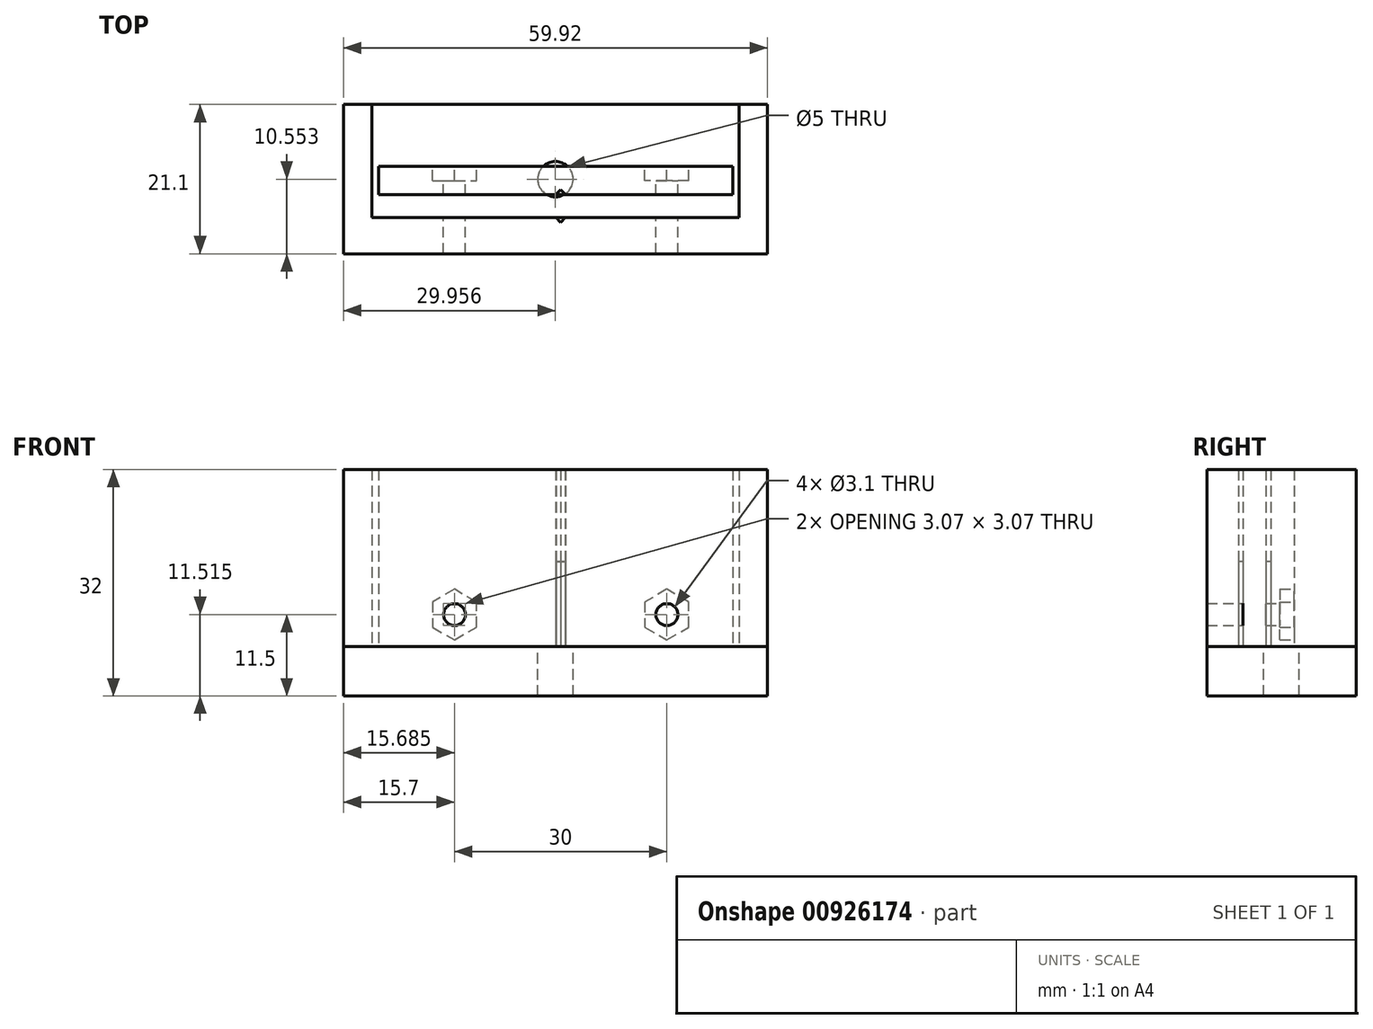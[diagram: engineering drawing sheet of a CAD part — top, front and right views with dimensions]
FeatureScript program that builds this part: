
annotation { "Feature Type Name" : "Feature", "Feature Type Description" : "" }
export const myFeature = defineFeature(function(context is Context, id is Id, definition is map)
    precondition{}
    {
        {
            var Q0;
            Q0=qCreatedBy(makeId("Top.planeOp"),FACE);
            var sketch = newSketch(context, id + "F0", { "sketchPlane" : qUnion([Q0])});
            skLineSegment(sketch, "E0.bottom", {"start": v(0, 1.43) * mm, "end": v(-0.7, 0.72) * mm});
            skLineSegment(sketch, "E0.top", {"start": v(0.7, 0.72) * mm, "end": v(0.7, 0.72) * mm});
            skLineSegment(sketch, "E0.left", {"start": v(0, 1.43) * mm, "end": v(0.7, 0.72) * mm});
            skLineSegment(sketch, "E0.right", {"start": v(-0.7, 0.72) * mm, "end": v(-0.7, 0.72) * mm});
            skLineSegment(sketch, "E1.bottom", {"start": v(24.3, 4.72) * mm, "end": v(-25.7, 4.72) * mm});
            skLineSegment(sketch, "E1.left", {"start": v(24.3, 4.72) * mm, "end": v(24.3, 0.72) * mm});
            skLineSegment(sketch, "E1.right", {"start": v(-25.7, 4.72) * mm, "end": v(-25.7, 0.71) * mm});
            skLineSegment(sketch, "E2", {"start": v(-25.7, 0.71) * mm, "end": v(-0.7, 0.72) * mm});
            skPoint(sketch, "E3", {"position": v(24.3, 0.72) * mm});
            skLineSegment(sketch, "E4.trimOffspring", {"start": v(0.7, 0.72) * mm, "end": v(24.3, 0.72) * mm});
            skPoint(sketch, "E5.orphan", {"position": v(0, -0.2) * mm});
            skPoint(sketch, "E6.orphan", {"position": v(24.3, 9.1) * mm});
            skLineSegment(sketch, "E7.bottom", {"start": v(-0.64, -2.52) * mm, "end": v(0, -3.17) * mm});
            skLineSegment(sketch, "E7.right", {"start": v(0, -3.17) * mm, "end": v(0.64, -2.52) * mm});
            skLineSegment(sketch, "E8.bottom", {"start": v(23, -2.52) * mm, "end": v(0.64, -2.52) * mm});
            skPoint(sketch, "E8.middle", {"position": v(-3, -4.02) * mm});
            skLineSegment(sketch, "E9.top", {"start": v(-30.7, 13.48) * mm, "end": v(-26.7, 13.48) * mm});
            skLineSegment(sketch, "E9.left", {"start": v(-30.7, -2.52) * mm, "end": v(-30.7, 13.48) * mm});
            skLineSegment(sketch, "E9.right", {"start": v(-26.7, -2.52) * mm, "end": v(-26.7, 13.48) * mm});
            skLineSegment(sketch, "E10.top", {"start": v(29.2, 13.48) * mm, "end": v(25.2, 13.48) * mm});
            skLineSegment(sketch, "E10.left", {"start": v(29.2, -2.52) * mm, "end": v(29.2, 13.48) * mm});
            skLineSegment(sketch, "E10.right", {"start": v(25.2, -2.52) * mm, "end": v(25.2, 13.48) * mm});
            skPoint(sketch, "E11", {"position": v(0.64, -2.52) * mm});
            skPoint(sketch, "E12", {"position": v(-0.64, -2.52) * mm});
            skLineSegment(sketch, "E13", {"start": v(23, -2.52) * mm, "end": v(25.2, -2.52) * mm});
            skLineSegment(sketch, "E14", {"start": v(-26.7, -2.52) * mm, "end": v(-0.64, -2.52) * mm});
            skLineSegment(sketch, "E15", {"start": v(-30.7, -2.52) * mm, "end": v(-30.7, -7.62) * mm});
            skLineSegment(sketch, "E16", {"start": v(-30.7, -7.62) * mm, "end": v(29.22, -7.62) * mm});
            skLineSegment(sketch, "E17", {"start": v(29.22, -7.62) * mm, "end": v(29.2, -2.52) * mm});
            skLineSegment(sketch, "E18", {"start": v(0.7, 0.72) * mm, "end": v(-0.7, 0.72) * mm});
            skLineSegment(sketch, "E19", {"start": v(-0.64, -2.52) * mm, "end": v(0.64, -2.52) * mm});
            skSolve(sketch);
        }
        {
            var Q0;
            Q0=makeQuery(id+"F0.imprint","IMPRINT",FACE,{"disambiguationData":[TD([[makeQuery(id+"F0.imprint","IMPRINT",EDGE,{"derivedFrom":sQuery(id+"F0.wireOp",EDGE,"E7.bottom")}),-1.0]])]});
            var Q1;
            Q1=makeQuery(id+"F0.imprint","IMPRINT",FACE,{"disambiguationData":[TD([[makeQuery(id+"F0.imprint","IMPRINT",EDGE,{"derivedFrom":sQuery(id+"F0.wireOp",EDGE,"E0.bottom")}),-1.0]])]});
            extrude(context, id + "F1", {"entities" : qUnion([Q0, Q1]), "depth" : 25 * mm, "offsetDistance" : 25 * mm});
        }
        {
            var Q0;
            Q0=makeQuery(id+"F1.opExtrude","SWEPT_FACE",FACE,{"disambiguationData":[OSD([sQuery(id+"F0.wireOp",EDGE,"E1.bottom")])]});
            var sketch = newSketch(context, id + "F2", { "sketchPlane" : qUnion([Q0])});
            skLineSegment(sketch, "E20", {"start": v(0.7, 0) * mm, "end": v(0.7, 25) * mm});
            skLineSegment(sketch, "E21", {"start": v(0.7, 12.5) * mm, "end": v(15.7, 12.5) * mm});
            skLineSegment(sketch, "E22", {"start": v(0.7, 12.5) * mm, "end": v(-14.3, 12.5) * mm});
            skCircle(sketch, "E23", {"center": v(15, 4.5) * mm, "radius": 1.55 * mm});
            skCircle(sketch, "E24", {"center": v(-15, 4.5) * mm, "radius": 1.55 * mm});
            skCircle(sketch, "E25.cCircle", {"center": v(15, 4.5) * mm, "radius": 3.1 * mm, "construction": true});
            skLineSegment(sketch, "E25.0", {"start": v(11.9, 2.71) * mm, "end": v(11.9, 6.29) * mm});
            skLineSegment(sketch, "E25.1", {"start": v(11.9, 6.29) * mm, "end": v(15, 8.08) * mm});
            skLineSegment(sketch, "E25.2", {"start": v(15, 8.08) * mm, "end": v(18.1, 6.29) * mm});
            skLineSegment(sketch, "E25.3", {"start": v(18.1, 6.29) * mm, "end": v(18.1, 2.71) * mm});
            skLineSegment(sketch, "E25.4", {"start": v(18.1, 2.71) * mm, "end": v(15, 0.92) * mm});
            skLineSegment(sketch, "E25.5", {"start": v(15, 0.92) * mm, "end": v(11.9, 2.71) * mm});
            skPoint(sketch, "E25.0.midPoint", {"position": v(11.9, 4.5) * mm});
            skCircle(sketch, "E26.cCircle", {"center": v(-15, 4.5) * mm, "radius": 3.1 * mm, "construction": true});
            skLineSegment(sketch, "E26.0", {"start": v(-11.9, 6.29) * mm, "end": v(-11.9, 2.71) * mm});
            skLineSegment(sketch, "E26.1", {"start": v(-11.9, 2.71) * mm, "end": v(-15, 0.92) * mm});
            skLineSegment(sketch, "E26.2", {"start": v(-15, 0.92) * mm, "end": v(-18.1, 2.71) * mm});
            skLineSegment(sketch, "E26.3", {"start": v(-18.1, 2.71) * mm, "end": v(-18.1, 6.29) * mm});
            skLineSegment(sketch, "E26.4", {"start": v(-18.1, 6.29) * mm, "end": v(-15, 8.08) * mm});
            skLineSegment(sketch, "E26.5", {"start": v(-15, 8.08) * mm, "end": v(-11.9, 6.29) * mm});
            skPoint(sketch, "E26.0.midPoint", {"position": v(-11.9, 4.5) * mm});
            skSolve(sketch);
        }
        {
            var Q0;
            Q0=makeQuery(id+"F2.imprint","IMPRINT",FACE,{"disambiguationData":[TD([[makeQuery(id+"F2.imprint","IMPRINT",EDGE,{"derivedFrom":sQuery(id+"F2.wireOp",EDGE,"E24")}),-1.0]])]});
            var Q1;
            Q1=makeQuery(id+"F2.imprint","IMPRINT",FACE,{"disambiguationData":[TD([[makeQuery(id+"F2.imprint","IMPRINT",EDGE,{"derivedFrom":sQuery(id+"F2.wireOp",EDGE,"E23")}),-1.0]])]});
            extrude(context, id + "F3", {"entities" : qUnion([Q0, Q1]), "operationType" : NewBodyOperationType.REMOVE, "oppositeDirection" : true, "depth" : 2 * mm, "offsetDistance" : 25 * mm});
        }
        {
            var Q0;
            Q0=makeQuery(id+"F3.boolean.opBoolean","SPLIT",FACE,{"disambiguationData":[TD([makeQuery(id+"F3.opExtrude","SWEPT_FACE",FACE,{"disambiguationData":[OSD([sQuery(id+"F2.wireOp",EDGE,"E23")])]})])],"derivedFrom":makeQuery(id+"F1.opExtrude","SWEPT_FACE",FACE,{"disambiguationData":[OSD([sQuery(id+"F0.wireOp",EDGE,"E1.bottom")])]})});
            var Q1;
            Q1=makeQuery(id+"F3.boolean.opBoolean","SPLIT",FACE,{"disambiguationData":[TD([makeQuery(id+"F3.opExtrude","SWEPT_FACE",FACE,{"disambiguationData":[OSD([sQuery(id+"F2.wireOp",EDGE,"E24")])]})])],"derivedFrom":makeQuery(id+"F1.opExtrude","SWEPT_FACE",FACE,{"disambiguationData":[OSD([sQuery(id+"F0.wireOp",EDGE,"E1.bottom")])]})});
            extrude(context, id + "F4", {"entities" : qUnion([Q0, Q1]), "operationType" : NewBodyOperationType.REMOVE, "oppositeDirection" : true, "depth" : 25 * mm, "offsetDistance" : 25 * mm});
        }
        {
            var Q0;
            Q0=makeQuery(id+"F1.opExtrude","CAP_FACE",FACE,{"disambiguationData":[OSD([sQuery(id+"F0.wireOp",EDGE,"E7.bottom"),sQuery(id+"F0.wireOp",EDGE,"E7.top"),sQuery(id+"F0.wireOp",EDGE,"E7.left"),sQuery(id+"F0.wireOp",EDGE,"E7.right"),sQuery(id+"F0.wireOp",EDGE,"E8.bottom"),sQuery(id+"F0.wireOp",EDGE,"E8.left"),sQuery(id+"F0.wireOp",EDGE,"E8.right"),sQuery(id+"F0.wireOp",EDGE,"E9.top"),sQuery(id+"F0.wireOp",EDGE,"E9.left"),sQuery(id+"F0.wireOp",EDGE,"E9.right"),sQuery(id+"F0.wireOp",EDGE,"E10.top"),sQuery(id+"F0.wireOp",EDGE,"E10.left"),sQuery(id+"F0.wireOp",EDGE,"E10.right"),sQuery(id+"F0.wireOp",EDGE,"oWC5LRSD-4os8-z2Fm-aTpU-MEdmSwmbhTo2.bottom"),sQuery(id+"F0.wireOp",EDGE,"oWC5LRSD-4os8-z2Fm-aTpU-MEdmSwmbhTo2.top"),sQuery(id+"F0.wireOp",EDGE,"oWC5LRSD-4os8-z2Fm-aTpU-MEdmSwmbhTo2.left"),sQuery(id+"F0.wireOp",EDGE,"oWC5LRSD-4os8-z2Fm-aTpU-MEdmSwmbhTo2.right"),sQuery(id+"F0.wireOp",EDGE,"5714eec2-5c47-4e83-968c-a4c1f0155401.trimOffspring")])],"isStart":true});
            var sketch = newSketch(context, id + "F5", { "sketchPlane" : qUnion([Q0])});
            skLineSegment(sketch, "E27.bottom", {"start": v(-30.7, 7.62) * mm, "end": v(29.2, 7.62) * mm});
            skLineSegment(sketch, "E27.top", {"start": v(-30.7, -13.48) * mm, "end": v(29.2, -13.48) * mm});
            skLineSegment(sketch, "E27.left", {"start": v(-30.7, 7.62) * mm, "end": v(-30.7, -13.48) * mm});
            skLineSegment(sketch, "E27.right", {"start": v(29.2, 7.62) * mm, "end": v(29.2, -13.48) * mm});
            skLineSegment(sketch, "E28", {"start": v(-30.7, -13.48) * mm, "end": v(29.22, 7.62) * mm});
            skLineSegment(sketch, "E29", {"start": v(-30.7, 7.62) * mm, "end": v(29.2, -13.48) * mm});
            skPoint(sketch, "E30", {"position": v(-0.74, -2.93) * mm});
            skCircle(sketch, "E31", {"center": v(-0.74, -2.93) * mm, "radius": 2.5 * mm});
            skSolve(sketch);
        }
        {
            var Q0;
            Q0 = qSketchRegion(id + "F5", true);
            extrude(context, id + "F6", {"entities" : qUnion([Q0]), "depth" : 7 * mm, "offsetDistance" : 25 * mm});
        }
        {
            var Q0;
            Q0=makeQuery(id+"F0.imprint","IMPRINT",FACE,{"disambiguationData":[TD([[makeQuery(id+"F0.imprint","IMPRINT",EDGE,{"derivedFrom":sQuery(id+"F0.wireOp",EDGE,"E0.bottom")}),1.0]])]});
            var Q1;
            Q1=makeQuery(id+"F0.imprint","IMPRINT",FACE,{"disambiguationData":[TD([[makeQuery(id+"F0.imprint","IMPRINT",EDGE,{"derivedFrom":sQuery(id+"F0.wireOp",EDGE,"E7.bottom")}),1.0]])]});
            extrude(context, id + "F7", {"entities" : qUnion([Q0, Q1]), "depth" : 12 * mm, "offsetDistance" : 25 * mm});
        }
    });
